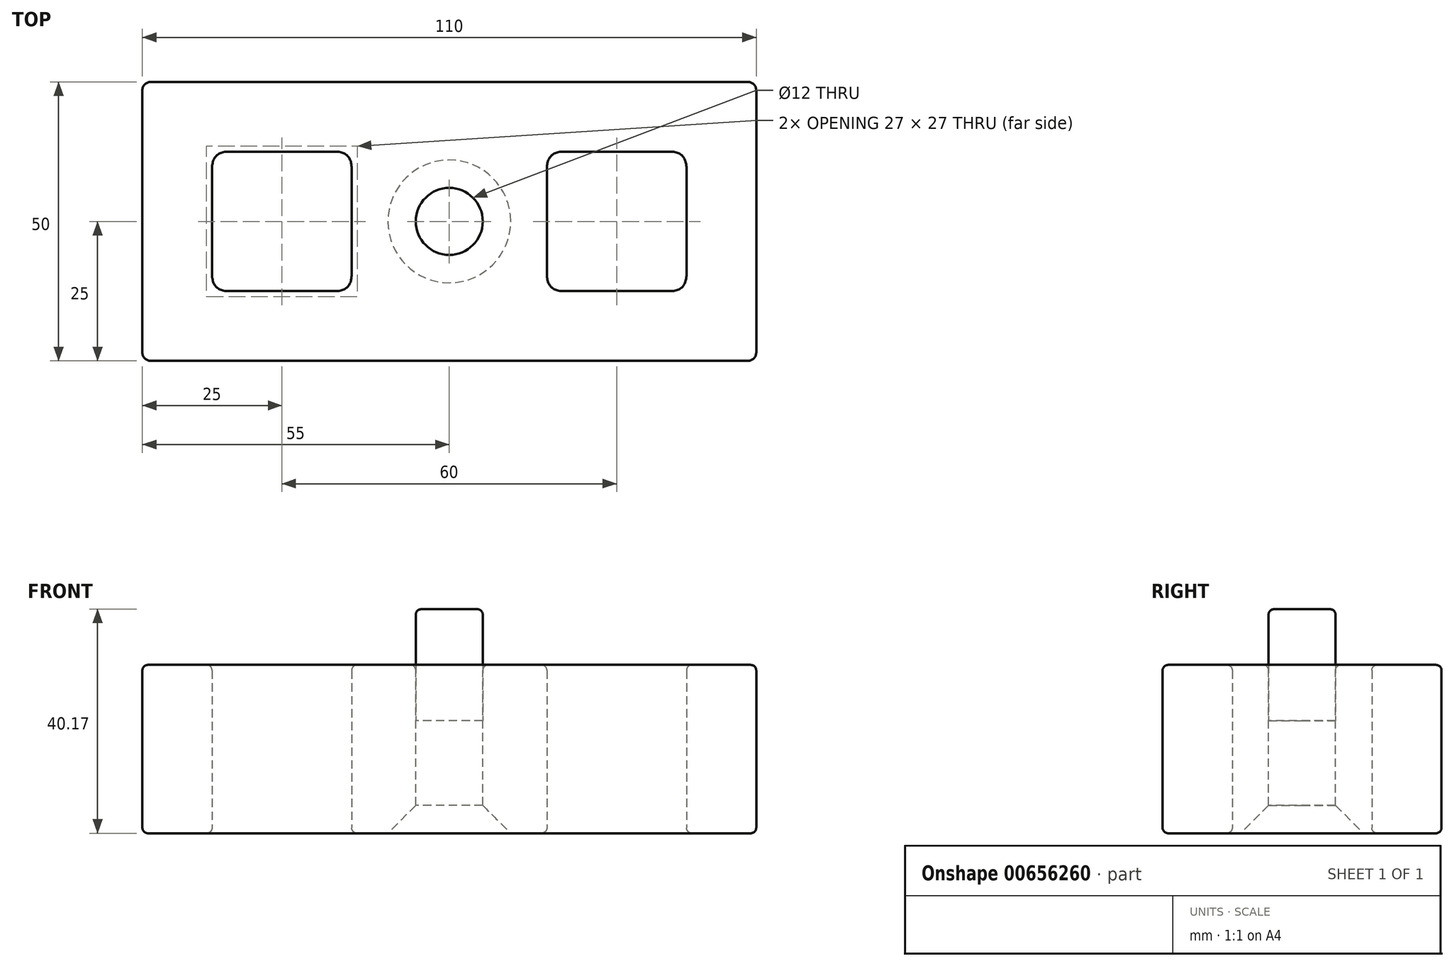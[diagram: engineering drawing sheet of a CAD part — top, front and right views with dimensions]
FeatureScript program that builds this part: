
annotation { "Feature Type Name" : "Feature", "Feature Type Description" : "" }
export const myFeature = defineFeature(function(context is Context, id is Id, definition is map)
    precondition{}
    {
        {
            var Q0;
            Q0=qCreatedBy(makeId("Top.planeOp"),FACE);
            var sketch = newSketch(context, id + "F0", { "sketchPlane" : qUnion([Q0])});
            skLineSegment(sketch, "E0.bottom", {"start": v(55, 25) * mm, "end": v(-55, 25) * mm});
            skLineSegment(sketch, "E0.top", {"start": v(55, -25) * mm, "end": v(-55, -25) * mm});
            skLineSegment(sketch, "E0.left", {"start": v(55, 25) * mm, "end": v(55, -25) * mm});
            skLineSegment(sketch, "E0.right", {"start": v(-55, 25) * mm, "end": v(-55, -25) * mm});
            skPoint(sketch, "E0.middle", {"position": v(0, 0) * mm});
            skCircle(sketch, "E1", {"center": v(0, 0) * mm, "radius": 6 * mm});
            skLineSegment(sketch, "E2.bottom", {"start": v(-42.5, 12.5) * mm, "end": v(-17.5, 12.5) * mm});
            skLineSegment(sketch, "E2.top", {"start": v(-42.5, -12.5) * mm, "end": v(-17.5, -12.5) * mm});
            skLineSegment(sketch, "E2.left", {"start": v(-42.5, 12.5) * mm, "end": v(-42.5, -12.5) * mm});
            skLineSegment(sketch, "E2.right", {"start": v(-17.5, 12.5) * mm, "end": v(-17.5, -12.5) * mm});
            skLineSegment(sketch, "E3.bottom", {"start": v(17.5, 12.5) * mm, "end": v(42.5, 12.5) * mm});
            skLineSegment(sketch, "E3.top", {"start": v(17.5, -12.5) * mm, "end": v(42.5, -12.5) * mm});
            skLineSegment(sketch, "E3.left", {"start": v(17.5, 12.5) * mm, "end": v(17.5, -12.5) * mm});
            skLineSegment(sketch, "E3.right", {"start": v(42.5, 12.5) * mm, "end": v(42.5, -12.5) * mm});
            skSolve(sketch);
        }
        {
            var Q0;
            Q0=makeQuery(id+"F0.imprint","IMPRINT",FACE,{"disambiguationData":[TD([[makeQuery(id+"F0.imprint","IMPRINT",EDGE,{"derivedFrom":sQuery(id+"F0.wireOp",EDGE,"E1")}),1.0]])]});
            extrude(context, id + "F1", {"entities" : qUnion([Q0]), "endBound" : BoundingType.SYMMETRIC, "depth" : 20 * mm, "offsetDistance" : 25 * mm});
        }
        {
            var Q0;
            Q0 = qSketchRegion(id + "F0", true);
            extrude(context, id + "F2", {"entities" : qUnion([Q0]), "oppositeDirection" : true, "depth" : 30.17 * mm, "offsetDistance" : 25 * mm});
        }
        {
            var Q0;
            Q0=makeQuery(id+"F2.opExtrude","CAP_EDGE",EDGE,{"disambiguationData":[OSD([sQuery(id+"F0.wireOp",EDGE,"E1")])],"isStart":false});
            chamfer(context, id + "F3", {"entities" : qUnion([Q0]), "width" : 5 * mm, "tangentPropagation" : true});
        }
        {
            var Q0;
            Q0=makeQuery(id+"F2.opExtrude","SWEPT_EDGE",EDGE,{"disambiguationData":[OSD([sQuery(id+"F0.wireOp",EDGE,"E2.bottom"),sQuery(id+"F0.wireOp",EDGE,"E2.left")])]});
            var Q1;
            Q1=makeQuery(id+"F2.opExtrude","SWEPT_EDGE",EDGE,{"disambiguationData":[OSD([sQuery(id+"F0.wireOp",EDGE,"E2.bottom"),sQuery(id+"F0.wireOp",EDGE,"E2.right")])]});
            var Q2;
            Q2=makeQuery(id+"F2.opExtrude","SWEPT_EDGE",EDGE,{"disambiguationData":[OSD([sQuery(id+"F0.wireOp",EDGE,"E2.top"),sQuery(id+"F0.wireOp",EDGE,"E2.right")])]});
            var Q3;
            Q3=makeQuery(id+"F2.opExtrude","SWEPT_EDGE",EDGE,{"disambiguationData":[OSD([sQuery(id+"F0.wireOp",EDGE,"E2.top"),sQuery(id+"F0.wireOp",EDGE,"E2.left")])]});
            var Q4;
            Q4=makeQuery(id+"F2.opExtrude","SWEPT_EDGE",EDGE,{"disambiguationData":[OSD([sQuery(id+"F0.wireOp",EDGE,"E3.top"),sQuery(id+"F0.wireOp",EDGE,"E3.left")])]});
            var Q5;
            Q5=makeQuery(id+"F2.opExtrude","SWEPT_EDGE",EDGE,{"disambiguationData":[OSD([sQuery(id+"F0.wireOp",EDGE,"E3.top"),sQuery(id+"F0.wireOp",EDGE,"E3.right")])]});
            var Q6;
            Q6=makeQuery(id+"F2.opExtrude","SWEPT_EDGE",EDGE,{"disambiguationData":[OSD([sQuery(id+"F0.wireOp",EDGE,"E3.bottom"),sQuery(id+"F0.wireOp",EDGE,"E3.right")])]});
            var Q7;
            Q7=makeQuery(id+"F2.opExtrude","SWEPT_EDGE",EDGE,{"disambiguationData":[OSD([sQuery(id+"F0.wireOp",EDGE,"E3.bottom"),sQuery(id+"F0.wireOp",EDGE,"E3.left")])]});
            fillet(context, id + "F4", {"entities" : qUnion([Q0, Q1, Q2, Q3, Q4, Q5, Q6, Q7]), "radius" : 3 * mm, "tangentPropagation" : true, "rho" : 0.5, "crossSection" : FilletCrossSection.CONIC, "allowEdgeOverflow" : false});
        }
        {
            var Q0;
            Q0=makeQuery(id+"F2.opExtrude","SWEPT_EDGE",EDGE,{"disambiguationData":[OSD([sQuery(id+"F0.wireOp",EDGE,"E0.bottom"),sQuery(id+"F0.wireOp",EDGE,"E0.left")])]});
            var Q1;
            Q1=makeQuery(id+"F2.opExtrude","SWEPT_EDGE",EDGE,{"disambiguationData":[OSD([sQuery(id+"F0.wireOp",EDGE,"E0.top"),sQuery(id+"F0.wireOp",EDGE,"E0.left")])]});
            var Q2;
            Q2=makeQuery(id+"F2.opExtrude","SWEPT_EDGE",EDGE,{"disambiguationData":[OSD([sQuery(id+"F0.wireOp",EDGE,"E0.bottom"),sQuery(id+"F0.wireOp",EDGE,"E0.right")])]});
            var Q3;
            Q3=makeQuery(id+"F2.opExtrude","SWEPT_EDGE",EDGE,{"disambiguationData":[OSD([sQuery(id+"F0.wireOp",EDGE,"E0.top"),sQuery(id+"F0.wireOp",EDGE,"E0.right")])]});
            fillet(context, id + "F5", {"entities" : qUnion([Q0, Q1, Q2, Q3]), "radius" : 1.5 * mm, "tangentPropagation" : true, "allowEdgeOverflow" : false});
        }
        {
            var Q0;
            Q0=makeQuery(id+"F1.opExtrude","CAP_EDGE",EDGE,{"disambiguationData":[OSD([sQuery(id+"F0.wireOp",EDGE,"E1")])],"isStart":false});
            var Q1;
            Q1=makeQuery(id+"F2.opExtrude","CAP_FACE",FACE,{"disambiguationData":[OSD([sQuery(id+"F0.wireOp",EDGE,"E0.bottom"),sQuery(id+"F0.wireOp",EDGE,"E0.top"),sQuery(id+"F0.wireOp",EDGE,"E0.left"),sQuery(id+"F0.wireOp",EDGE,"E0.right"),sQuery(id+"F0.wireOp",EDGE,"E1"),sQuery(id+"F0.wireOp",EDGE,"E2.bottom"),sQuery(id+"F0.wireOp",EDGE,"E2.top"),sQuery(id+"F0.wireOp",EDGE,"E2.left"),sQuery(id+"F0.wireOp",EDGE,"E2.right"),sQuery(id+"F0.wireOp",EDGE,"E3.bottom"),sQuery(id+"F0.wireOp",EDGE,"E3.top"),sQuery(id+"F0.wireOp",EDGE,"E3.left"),sQuery(id+"F0.wireOp",EDGE,"E3.right")])],"isStart":true});
            fillet(context, id + "F6", {"entities" : qUnion([Q0, Q1]), "radius" : 1 * mm, "tangentPropagation" : true, "allowEdgeOverflow" : false});
        }
        {
            var Q0;
            Q0=makeQuery(id+"F2.opExtrude","CAP_EDGE",EDGE,{"disambiguationData":[OSD([sQuery(id+"F0.wireOp",EDGE,"E0.top")])],"isStart":false});
            var Q1;
            Q1=makeQuery(id+"F2.opExtrude","CAP_EDGE",EDGE,{"disambiguationData":[OSD([sQuery(id+"F0.wireOp",EDGE,"E0.left")])],"isStart":false});
            var Q2;
            Q2=makeQuery(id+"F2.opExtrude","CAP_EDGE",EDGE,{"disambiguationData":[OSD([sQuery(id+"F0.wireOp",EDGE,"E0.bottom")])],"isStart":false});
            var Q3;
            Q3=makeQuery(id+"F2.opExtrude","CAP_EDGE",EDGE,{"disambiguationData":[OSD([sQuery(id+"F0.wireOp",EDGE,"E0.right")])],"isStart":false});
            fillet(context, id + "F7", {"entities" : qUnion([Q0, Q1, Q2, Q3]), "radius" : 1 * mm, "tangentPropagation" : true, "allowEdgeOverflow" : false});
        }
        {
            var Q0;
            Q0=makeQuery(id+"F2.opExtrude","CAP_EDGE",EDGE,{"disambiguationData":[OSD([sQuery(id+"F0.wireOp",EDGE,"E2.right")])],"isStart":false});
            var Q1;
            Q1=makeQuery(id+"F2.opExtrude","CAP_EDGE",EDGE,{"disambiguationData":[OSD([sQuery(id+"F0.wireOp",EDGE,"E2.bottom")])],"isStart":false});
            var Q2;
            Q2=makeQuery(id+"F2.opExtrude","CAP_EDGE",EDGE,{"disambiguationData":[OSD([sQuery(id+"F0.wireOp",EDGE,"E2.left")])],"isStart":false});
            var Q3;
            Q3=makeQuery(id+"F2.opExtrude","CAP_EDGE",EDGE,{"disambiguationData":[OSD([sQuery(id+"F0.wireOp",EDGE,"E2.top")])],"isStart":false});
            var Q4;
            Q4=makeQuery(id+"F2.opExtrude","CAP_EDGE",EDGE,{"disambiguationData":[OSD([sQuery(id+"F0.wireOp",EDGE,"E3.left")])],"isStart":false});
            var Q5;
            Q5=makeQuery(id+"F2.opExtrude","CAP_EDGE",EDGE,{"disambiguationData":[OSD([sQuery(id+"F0.wireOp",EDGE,"E3.bottom")])],"isStart":false});
            var Q6;
            Q6=makeQuery(id+"F2.opExtrude","CAP_EDGE",EDGE,{"disambiguationData":[OSD([sQuery(id+"F0.wireOp",EDGE,"E3.right")])],"isStart":false});
            var Q7;
            Q7=makeQuery(id+"F2.opExtrude","CAP_EDGE",EDGE,{"disambiguationData":[OSD([sQuery(id+"F0.wireOp",EDGE,"E3.top")])],"isStart":false});
            var Q8;
            {var subQ0=sQuery(id+"F0.wireOp",EDGE,"E3.left");var subQ1=sQuery(id+"F0.wireOp",EDGE,"E3.bottom");Q8=makeQuery(id+"F4.opFillet","BLEND_EDGE",EDGE,{"blendedFrom":[makeQuery(id+"F2.opExtrude","SWEPT_EDGE",EDGE,{"disambiguationData":[OSD([subQ1,subQ0])]}),makeQuery(id+"F2.opExtrude","CAP_FACE",FACE,{"disambiguationData":[OSD([sQuery(id+"F0.wireOp",EDGE,"E0.bottom"),sQuery(id+"F0.wireOp",EDGE,"E0.top"),sQuery(id+"F0.wireOp",EDGE,"E0.left"),sQuery(id+"F0.wireOp",EDGE,"E0.right"),sQuery(id+"F0.wireOp",EDGE,"E1"),sQuery(id+"F0.wireOp",EDGE,"E2.bottom"),sQuery(id+"F0.wireOp",EDGE,"E2.top"),sQuery(id+"F0.wireOp",EDGE,"E2.left"),sQuery(id+"F0.wireOp",EDGE,"E2.right"),subQ1,sQuery(id+"F0.wireOp",EDGE,"E3.top"),subQ0,sQuery(id+"F0.wireOp",EDGE,"E3.right")])],"isStart":false})],"blendedInto":[makeQuery(id+"F2.opExtrude","CAP_FACE",FACE,{"disambiguationData":[OSD([sQuery(id+"F0.wireOp",EDGE,"E0.bottom"),sQuery(id+"F0.wireOp",EDGE,"E0.top"),sQuery(id+"F0.wireOp",EDGE,"E0.left"),sQuery(id+"F0.wireOp",EDGE,"E0.right"),sQuery(id+"F0.wireOp",EDGE,"E1"),sQuery(id+"F0.wireOp",EDGE,"E2.bottom"),sQuery(id+"F0.wireOp",EDGE,"E2.top"),sQuery(id+"F0.wireOp",EDGE,"E2.left"),sQuery(id+"F0.wireOp",EDGE,"E2.right"),subQ1,sQuery(id+"F0.wireOp",EDGE,"E3.top"),subQ0,sQuery(id+"F0.wireOp",EDGE,"E3.right")])],"isStart":false})]});}
            var Q9;
            {var subQ0=sQuery(id+"F0.wireOp",EDGE,"E3.right");var subQ1=sQuery(id+"F0.wireOp",EDGE,"E3.bottom");Q9=makeQuery(id+"F4.opFillet","BLEND_EDGE",EDGE,{"blendedFrom":[makeQuery(id+"F2.opExtrude","SWEPT_EDGE",EDGE,{"disambiguationData":[OSD([subQ1,subQ0])]}),makeQuery(id+"F2.opExtrude","CAP_FACE",FACE,{"disambiguationData":[OSD([sQuery(id+"F0.wireOp",EDGE,"E0.bottom"),sQuery(id+"F0.wireOp",EDGE,"E0.top"),sQuery(id+"F0.wireOp",EDGE,"E0.left"),sQuery(id+"F0.wireOp",EDGE,"E0.right"),sQuery(id+"F0.wireOp",EDGE,"E1"),sQuery(id+"F0.wireOp",EDGE,"E2.bottom"),sQuery(id+"F0.wireOp",EDGE,"E2.top"),sQuery(id+"F0.wireOp",EDGE,"E2.left"),sQuery(id+"F0.wireOp",EDGE,"E2.right"),subQ1,sQuery(id+"F0.wireOp",EDGE,"E3.top"),sQuery(id+"F0.wireOp",EDGE,"E3.left"),subQ0])],"isStart":false})],"blendedInto":[makeQuery(id+"F2.opExtrude","CAP_FACE",FACE,{"disambiguationData":[OSD([sQuery(id+"F0.wireOp",EDGE,"E0.bottom"),sQuery(id+"F0.wireOp",EDGE,"E0.top"),sQuery(id+"F0.wireOp",EDGE,"E0.left"),sQuery(id+"F0.wireOp",EDGE,"E0.right"),sQuery(id+"F0.wireOp",EDGE,"E1"),sQuery(id+"F0.wireOp",EDGE,"E2.bottom"),sQuery(id+"F0.wireOp",EDGE,"E2.top"),sQuery(id+"F0.wireOp",EDGE,"E2.left"),sQuery(id+"F0.wireOp",EDGE,"E2.right"),subQ1,sQuery(id+"F0.wireOp",EDGE,"E3.top"),sQuery(id+"F0.wireOp",EDGE,"E3.left"),subQ0])],"isStart":false})]});}
            var Q10;
            {var subQ0=sQuery(id+"F0.wireOp",EDGE,"E3.right");var subQ1=sQuery(id+"F0.wireOp",EDGE,"E3.top");Q10=makeQuery(id+"F4.opFillet","BLEND_EDGE",EDGE,{"blendedFrom":[makeQuery(id+"F2.opExtrude","SWEPT_EDGE",EDGE,{"disambiguationData":[OSD([subQ1,subQ0])]}),makeQuery(id+"F2.opExtrude","CAP_FACE",FACE,{"disambiguationData":[OSD([sQuery(id+"F0.wireOp",EDGE,"E0.bottom"),sQuery(id+"F0.wireOp",EDGE,"E0.top"),sQuery(id+"F0.wireOp",EDGE,"E0.left"),sQuery(id+"F0.wireOp",EDGE,"E0.right"),sQuery(id+"F0.wireOp",EDGE,"E1"),sQuery(id+"F0.wireOp",EDGE,"E2.bottom"),sQuery(id+"F0.wireOp",EDGE,"E2.top"),sQuery(id+"F0.wireOp",EDGE,"E2.left"),sQuery(id+"F0.wireOp",EDGE,"E2.right"),sQuery(id+"F0.wireOp",EDGE,"E3.bottom"),subQ1,sQuery(id+"F0.wireOp",EDGE,"E3.left"),subQ0])],"isStart":false})],"blendedInto":[makeQuery(id+"F2.opExtrude","CAP_FACE",FACE,{"disambiguationData":[OSD([sQuery(id+"F0.wireOp",EDGE,"E0.bottom"),sQuery(id+"F0.wireOp",EDGE,"E0.top"),sQuery(id+"F0.wireOp",EDGE,"E0.left"),sQuery(id+"F0.wireOp",EDGE,"E0.right"),sQuery(id+"F0.wireOp",EDGE,"E1"),sQuery(id+"F0.wireOp",EDGE,"E2.bottom"),sQuery(id+"F0.wireOp",EDGE,"E2.top"),sQuery(id+"F0.wireOp",EDGE,"E2.left"),sQuery(id+"F0.wireOp",EDGE,"E2.right"),sQuery(id+"F0.wireOp",EDGE,"E3.bottom"),subQ1,sQuery(id+"F0.wireOp",EDGE,"E3.left"),subQ0])],"isStart":false})]});}
            var Q11;
            {var subQ0=sQuery(id+"F0.wireOp",EDGE,"E3.left");var subQ1=sQuery(id+"F0.wireOp",EDGE,"E3.top");Q11=makeQuery(id+"F4.opFillet","BLEND_EDGE",EDGE,{"blendedFrom":[makeQuery(id+"F2.opExtrude","SWEPT_EDGE",EDGE,{"disambiguationData":[OSD([subQ1,subQ0])]}),makeQuery(id+"F2.opExtrude","CAP_FACE",FACE,{"disambiguationData":[OSD([sQuery(id+"F0.wireOp",EDGE,"E0.bottom"),sQuery(id+"F0.wireOp",EDGE,"E0.top"),sQuery(id+"F0.wireOp",EDGE,"E0.left"),sQuery(id+"F0.wireOp",EDGE,"E0.right"),sQuery(id+"F0.wireOp",EDGE,"E1"),sQuery(id+"F0.wireOp",EDGE,"E2.bottom"),sQuery(id+"F0.wireOp",EDGE,"E2.top"),sQuery(id+"F0.wireOp",EDGE,"E2.left"),sQuery(id+"F0.wireOp",EDGE,"E2.right"),sQuery(id+"F0.wireOp",EDGE,"E3.bottom"),subQ1,subQ0,sQuery(id+"F0.wireOp",EDGE,"E3.right")])],"isStart":false})],"blendedInto":[makeQuery(id+"F2.opExtrude","CAP_FACE",FACE,{"disambiguationData":[OSD([sQuery(id+"F0.wireOp",EDGE,"E0.bottom"),sQuery(id+"F0.wireOp",EDGE,"E0.top"),sQuery(id+"F0.wireOp",EDGE,"E0.left"),sQuery(id+"F0.wireOp",EDGE,"E0.right"),sQuery(id+"F0.wireOp",EDGE,"E1"),sQuery(id+"F0.wireOp",EDGE,"E2.bottom"),sQuery(id+"F0.wireOp",EDGE,"E2.top"),sQuery(id+"F0.wireOp",EDGE,"E2.left"),sQuery(id+"F0.wireOp",EDGE,"E2.right"),sQuery(id+"F0.wireOp",EDGE,"E3.bottom"),subQ1,subQ0,sQuery(id+"F0.wireOp",EDGE,"E3.right")])],"isStart":false})]});}
            var Q12;
            {var subQ0=sQuery(id+"F0.wireOp",EDGE,"E2.right");var subQ1=sQuery(id+"F0.wireOp",EDGE,"E2.top");Q12=makeQuery(id+"F4.opFillet","BLEND_EDGE",EDGE,{"blendedFrom":[makeQuery(id+"F2.opExtrude","SWEPT_EDGE",EDGE,{"disambiguationData":[OSD([subQ1,subQ0])]}),makeQuery(id+"F2.opExtrude","CAP_FACE",FACE,{"disambiguationData":[OSD([sQuery(id+"F0.wireOp",EDGE,"E0.bottom"),sQuery(id+"F0.wireOp",EDGE,"E0.top"),sQuery(id+"F0.wireOp",EDGE,"E0.left"),sQuery(id+"F0.wireOp",EDGE,"E0.right"),sQuery(id+"F0.wireOp",EDGE,"E1"),sQuery(id+"F0.wireOp",EDGE,"E2.bottom"),subQ1,sQuery(id+"F0.wireOp",EDGE,"E2.left"),subQ0,sQuery(id+"F0.wireOp",EDGE,"E3.bottom"),sQuery(id+"F0.wireOp",EDGE,"E3.top"),sQuery(id+"F0.wireOp",EDGE,"E3.left"),sQuery(id+"F0.wireOp",EDGE,"E3.right")])],"isStart":false})],"blendedInto":[makeQuery(id+"F2.opExtrude","CAP_FACE",FACE,{"disambiguationData":[OSD([sQuery(id+"F0.wireOp",EDGE,"E0.bottom"),sQuery(id+"F0.wireOp",EDGE,"E0.top"),sQuery(id+"F0.wireOp",EDGE,"E0.left"),sQuery(id+"F0.wireOp",EDGE,"E0.right"),sQuery(id+"F0.wireOp",EDGE,"E1"),sQuery(id+"F0.wireOp",EDGE,"E2.bottom"),subQ1,sQuery(id+"F0.wireOp",EDGE,"E2.left"),subQ0,sQuery(id+"F0.wireOp",EDGE,"E3.bottom"),sQuery(id+"F0.wireOp",EDGE,"E3.top"),sQuery(id+"F0.wireOp",EDGE,"E3.left"),sQuery(id+"F0.wireOp",EDGE,"E3.right")])],"isStart":false})]});}
            var Q13;
            {var subQ0=sQuery(id+"F0.wireOp",EDGE,"E2.right");var subQ1=sQuery(id+"F0.wireOp",EDGE,"E2.bottom");Q13=makeQuery(id+"F4.opFillet","BLEND_EDGE",EDGE,{"blendedFrom":[makeQuery(id+"F2.opExtrude","SWEPT_EDGE",EDGE,{"disambiguationData":[OSD([subQ1,subQ0])]}),makeQuery(id+"F2.opExtrude","CAP_FACE",FACE,{"disambiguationData":[OSD([sQuery(id+"F0.wireOp",EDGE,"E0.bottom"),sQuery(id+"F0.wireOp",EDGE,"E0.top"),sQuery(id+"F0.wireOp",EDGE,"E0.left"),sQuery(id+"F0.wireOp",EDGE,"E0.right"),sQuery(id+"F0.wireOp",EDGE,"E1"),subQ1,sQuery(id+"F0.wireOp",EDGE,"E2.top"),sQuery(id+"F0.wireOp",EDGE,"E2.left"),subQ0,sQuery(id+"F0.wireOp",EDGE,"E3.bottom"),sQuery(id+"F0.wireOp",EDGE,"E3.top"),sQuery(id+"F0.wireOp",EDGE,"E3.left"),sQuery(id+"F0.wireOp",EDGE,"E3.right")])],"isStart":false})],"blendedInto":[makeQuery(id+"F2.opExtrude","CAP_FACE",FACE,{"disambiguationData":[OSD([sQuery(id+"F0.wireOp",EDGE,"E0.bottom"),sQuery(id+"F0.wireOp",EDGE,"E0.top"),sQuery(id+"F0.wireOp",EDGE,"E0.left"),sQuery(id+"F0.wireOp",EDGE,"E0.right"),sQuery(id+"F0.wireOp",EDGE,"E1"),subQ1,sQuery(id+"F0.wireOp",EDGE,"E2.top"),sQuery(id+"F0.wireOp",EDGE,"E2.left"),subQ0,sQuery(id+"F0.wireOp",EDGE,"E3.bottom"),sQuery(id+"F0.wireOp",EDGE,"E3.top"),sQuery(id+"F0.wireOp",EDGE,"E3.left"),sQuery(id+"F0.wireOp",EDGE,"E3.right")])],"isStart":false})]});}
            var Q14;
            {var subQ0=sQuery(id+"F0.wireOp",EDGE,"E2.left");var subQ1=sQuery(id+"F0.wireOp",EDGE,"E2.bottom");Q14=makeQuery(id+"F4.opFillet","BLEND_EDGE",EDGE,{"blendedFrom":[makeQuery(id+"F2.opExtrude","SWEPT_EDGE",EDGE,{"disambiguationData":[OSD([subQ1,subQ0])]}),makeQuery(id+"F2.opExtrude","CAP_FACE",FACE,{"disambiguationData":[OSD([sQuery(id+"F0.wireOp",EDGE,"E0.bottom"),sQuery(id+"F0.wireOp",EDGE,"E0.top"),sQuery(id+"F0.wireOp",EDGE,"E0.left"),sQuery(id+"F0.wireOp",EDGE,"E0.right"),sQuery(id+"F0.wireOp",EDGE,"E1"),subQ1,sQuery(id+"F0.wireOp",EDGE,"E2.top"),subQ0,sQuery(id+"F0.wireOp",EDGE,"E2.right"),sQuery(id+"F0.wireOp",EDGE,"E3.bottom"),sQuery(id+"F0.wireOp",EDGE,"E3.top"),sQuery(id+"F0.wireOp",EDGE,"E3.left"),sQuery(id+"F0.wireOp",EDGE,"E3.right")])],"isStart":false})],"blendedInto":[makeQuery(id+"F2.opExtrude","CAP_FACE",FACE,{"disambiguationData":[OSD([sQuery(id+"F0.wireOp",EDGE,"E0.bottom"),sQuery(id+"F0.wireOp",EDGE,"E0.top"),sQuery(id+"F0.wireOp",EDGE,"E0.left"),sQuery(id+"F0.wireOp",EDGE,"E0.right"),sQuery(id+"F0.wireOp",EDGE,"E1"),subQ1,sQuery(id+"F0.wireOp",EDGE,"E2.top"),subQ0,sQuery(id+"F0.wireOp",EDGE,"E2.right"),sQuery(id+"F0.wireOp",EDGE,"E3.bottom"),sQuery(id+"F0.wireOp",EDGE,"E3.top"),sQuery(id+"F0.wireOp",EDGE,"E3.left"),sQuery(id+"F0.wireOp",EDGE,"E3.right")])],"isStart":false})]});}
            var Q15;
            {var subQ0=sQuery(id+"F0.wireOp",EDGE,"E2.left");var subQ1=sQuery(id+"F0.wireOp",EDGE,"E2.top");Q15=makeQuery(id+"F4.opFillet","BLEND_EDGE",EDGE,{"blendedFrom":[makeQuery(id+"F2.opExtrude","SWEPT_EDGE",EDGE,{"disambiguationData":[OSD([subQ1,subQ0])]}),makeQuery(id+"F2.opExtrude","CAP_FACE",FACE,{"disambiguationData":[OSD([sQuery(id+"F0.wireOp",EDGE,"E0.bottom"),sQuery(id+"F0.wireOp",EDGE,"E0.top"),sQuery(id+"F0.wireOp",EDGE,"E0.left"),sQuery(id+"F0.wireOp",EDGE,"E0.right"),sQuery(id+"F0.wireOp",EDGE,"E1"),sQuery(id+"F0.wireOp",EDGE,"E2.bottom"),subQ1,subQ0,sQuery(id+"F0.wireOp",EDGE,"E2.right"),sQuery(id+"F0.wireOp",EDGE,"E3.bottom"),sQuery(id+"F0.wireOp",EDGE,"E3.top"),sQuery(id+"F0.wireOp",EDGE,"E3.left"),sQuery(id+"F0.wireOp",EDGE,"E3.right")])],"isStart":false})],"blendedInto":[makeQuery(id+"F2.opExtrude","CAP_FACE",FACE,{"disambiguationData":[OSD([sQuery(id+"F0.wireOp",EDGE,"E0.bottom"),sQuery(id+"F0.wireOp",EDGE,"E0.top"),sQuery(id+"F0.wireOp",EDGE,"E0.left"),sQuery(id+"F0.wireOp",EDGE,"E0.right"),sQuery(id+"F0.wireOp",EDGE,"E1"),sQuery(id+"F0.wireOp",EDGE,"E2.bottom"),subQ1,subQ0,sQuery(id+"F0.wireOp",EDGE,"E2.right"),sQuery(id+"F0.wireOp",EDGE,"E3.bottom"),sQuery(id+"F0.wireOp",EDGE,"E3.top"),sQuery(id+"F0.wireOp",EDGE,"E3.left"),sQuery(id+"F0.wireOp",EDGE,"E3.right")])],"isStart":false})]});}
            fillet(context, id + "F8", {"entities" : qUnion([Q0, Q1, Q2, Q3, Q4, Q5, Q6, Q7, Q8, Q9, Q10, Q11, Q12, Q13, Q14, Q15]), "radius" : 1 * mm, "tangentPropagation" : true, "allowEdgeOverflow" : false});
        }
    });
